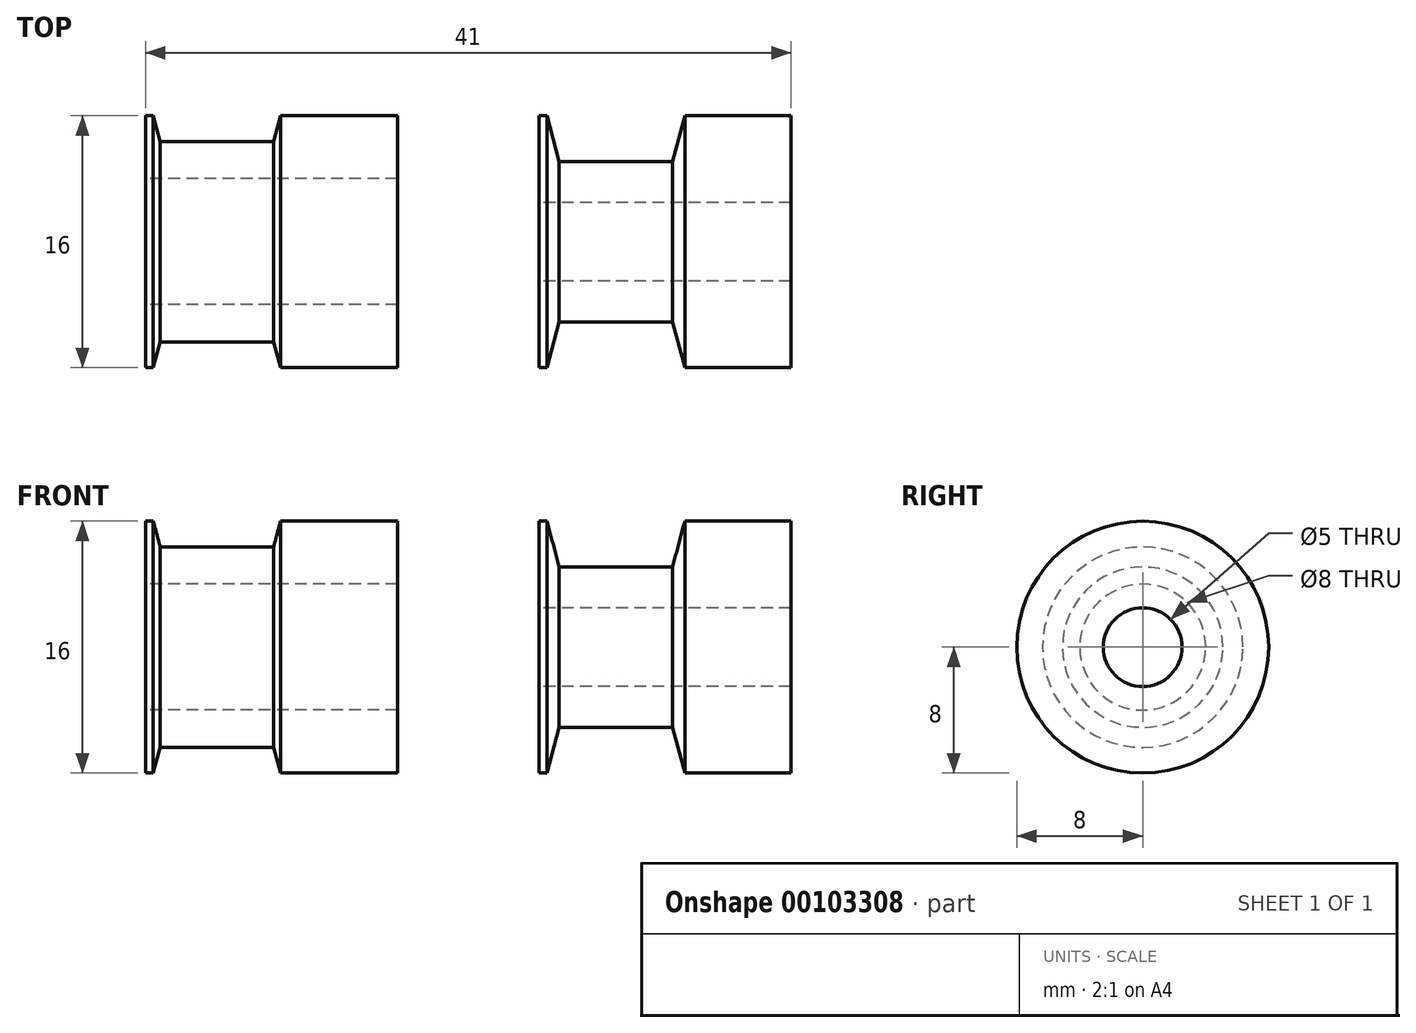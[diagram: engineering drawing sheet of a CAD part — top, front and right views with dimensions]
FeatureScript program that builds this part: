
annotation { "Feature Type Name" : "Feature", "Feature Type Description" : "" }
export const myFeature = defineFeature(function(context is Context, id is Id, definition is map)
    precondition{}
    {
        {
            var Q0;
            Q0=qCreatedBy(makeId("Front.planeOp"),FACE);
            var sketch = newSketch(context, id + "F0", { "sketchPlane" : qUnion([Q0])});
            skLineSegment(sketch, "E0.bottom", {"start": v(-3.56, 6.36) * mm, "end": v(3.64, 6.36) * mm});
            skLineSegment(sketch, "E1", {"start": v(-21.6, 0) * mm, "end": v(62.77, 0) * mm, "construction": true});
            skLineSegment(sketch, "E2.top", {"start": v(4.08, 8) * mm, "end": v(11.5, 8) * mm});
            skLineSegment(sketch, "E2.left", {"start": v(3.64, 6.37) * mm, "end": v(4.08, 8) * mm});
            skLineSegment(sketch, "E2.right", {"start": v(11.5, 4) * mm, "end": v(11.5, 8) * mm});
            skLineSegment(sketch, "E3.top", {"start": v(-4, 8) * mm, "end": v(-4.5, 8) * mm});
            skLineSegment(sketch, "E3.left", {"start": v(-3.56, 6.36) * mm, "end": v(-4, 8) * mm});
            skLineSegment(sketch, "E3.right", {"start": v(-4.5, 4) * mm, "end": v(-4.5, 8) * mm});
            skLineSegment(sketch, "E4", {"start": v(-4.5, 4) * mm, "end": v(11.5, 4) * mm});
            skLineSegment(sketch, "E5.bottom", {"start": v(20.5, 2.5) * mm, "end": v(36.5, 2.5) * mm});
            skLineSegment(sketch, "E5.top", {"start": v(20.5, 8) * mm, "end": v(21, 8) * mm});
            skLineSegment(sketch, "E5.left", {"start": v(20.5, 2.5) * mm, "end": v(20.5, 8) * mm});
            skLineSegment(sketch, "E5.right", {"start": v(36.5, 2.5) * mm, "end": v(36.5, 8) * mm});
            skLineSegment(sketch, "E6.top", {"start": v(21.78, 5.1) * mm, "end": v(28.98, 5.1) * mm});
            skLineSegment(sketch, "E6.left", {"start": v(21, 8) * mm, "end": v(21.78, 5.1) * mm});
            skLineSegment(sketch, "E6.right", {"start": v(29.76, 8) * mm, "end": v(28.98, 5.1) * mm});
            skLineSegment(sketch, "E7", {"start": v(25, 13.39) * mm, "end": v(25, -15) * mm, "construction": true});
            skLineSegment(sketch, "E8.trimOffspring", {"start": v(29.76, 8) * mm, "end": v(36.5, 8) * mm});
            skSolve(sketch);
        }
        {
            var Q0;
            Q0=makeQuery(id+"F0.imprint","IMPRINT",FACE,{"disambiguationData":[TD([[makeQuery(id+"F0.imprint","IMPRINT",EDGE,{"derivedFrom":sQuery(id+"F0.wireOp",EDGE,"E0.bottom")}),-1.0]])]});
            var Q1;
            Q1=sQuery(id+"F0.wireOp",EDGE,"E1");
            revolve(context, id + "F1", {"entities" : qUnion([Q0]), "axis" : qUnion([Q1]), "revolveType" : RevolveType.FULL});
        }
        {
            var Q0;
            Q0=makeQuery(id+"F0.imprint","IMPRINT",FACE,{"disambiguationData":[TD([[makeQuery(id+"F0.imprint","IMPRINT",EDGE,{"derivedFrom":sQuery(id+"F0.wireOp",EDGE,"E5.bottom")}),1.0]])]});
            var Q1;
            Q1=sQuery(id+"F0.wireOp",EDGE,"E1");
            revolve(context, id + "F2", {"entities" : qUnion([Q0]), "axis" : qUnion([Q1]), "revolveType" : RevolveType.FULL});
        }
    });
